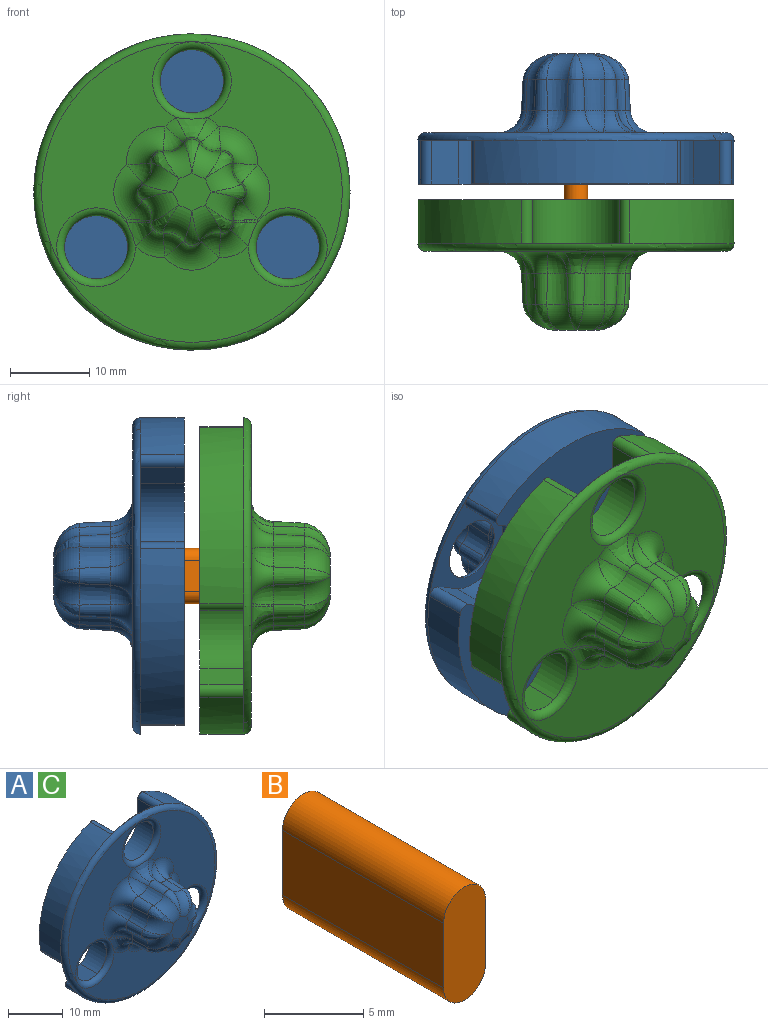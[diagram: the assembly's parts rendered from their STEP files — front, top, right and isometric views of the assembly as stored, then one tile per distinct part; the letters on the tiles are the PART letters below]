
ASSEMBLY  parts=3 mates=2
PART A: 99 faces, bbox 43.3x16.5x43.3 mm
  f0: plane 38.02x38.02mm, normal (0,-1,0), area 617.7mm2, adj f1,f47,f48,f49,f50,f89,f90,f91
  f1: torus R=4.39mm, axis (0,-1,0), area 1.4mm2, adj f0,f2,f45,f46
  f2: bspline ~3.03x2.86mm, area 5.2mm2, adj f1,f3,f47
  f3: cone r=2.36mm half-angle=3deg, axis (0,-1,0), area 11.4mm2, adj f2,f4,f44,f45
  f4: cone r=1.55mm half-angle=3deg, axis (0,1,0), area 9.6mm2, adj f3,f5,f42,f47
  f5: bspline ~4.27x3.32mm, area 5.5mm2, adj f4,f6,f44
  f6: torus R=6.21mm, axis (0,-1,0), area 14mm2, adj f5,f7,f41,f42
  f7: plane 4.83x4.83mm, normal (0,-1,0), area 15.8mm2, adj f6,f8,f35,f36,f37,f38,f39,f44
  f8: torus R=6.21mm, axis (0,-1,0), area 14mm2, adj f7,f9,f13,f14,f34
  f9: bspline ~3.02x2.67mm, area 3.8mm2, adj f8,f10,f39
  f10: cone r=1.55mm half-angle=3deg, axis (0,1,0), area 9.6mm2, adj f9,f11,f14,f95
  f11: cone r=2.36mm half-angle=3deg, axis (0,-1,0), area 11.4mm2, adj f10,f12,f39,f45
  f12: bspline ~3.03x2.86mm, area 5.2mm2, adj f11,f95,f96
  f13: bspline ~2.03x0.58mm, area 0.1mm2, adj f8,f39
  f14: cone r=2.36mm half-angle=3deg, axis (0,-1,0), area 11.4mm2, adj f8,f10,f15,f33
  f15: cone r=1.55mm half-angle=3deg, axis (0,1,0), area 9.6mm2, adj f14,f16,f17,f34,f92,f94
  f16: bspline ~4.05x3.8mm, area 7.7mm2, adj f15,f92,f93,f94
  f17: cone r=2.36mm half-angle=3deg, axis (0,-1,0), area 11.4mm2, adj f15,f18,f32,f35
  f18: cone r=1.55mm half-angle=3deg, axis (0,1,0), area 9.6mm2, adj f17,f19,f20,f91
  f19: bspline ~4.27x3.32mm, area 5.2mm2, adj f18,f35,f36
  f20: cone r=2.36mm half-angle=3deg, axis (0,-1,0), area 11.4mm2, adj f18,f21,f31,f36
  f21: cone r=1.55mm half-angle=3deg, axis (0,1,0), area 9.6mm2, adj f20,f22,f23,f90
  f22: bspline ~3.38x3.37mm, area 4.6mm2, adj f21,f36,f37
  f23: cone r=2.36mm half-angle=3deg, axis (0,-1,0), area 11.4mm2, adj f21,f24,f30,f37
  f24: cone r=1.55mm half-angle=3deg, axis (0,1,0), area 9.6mm2, adj f23,f25,f26,f27,f49,f89
  f25: bspline ~4.27x3.32mm, area 5.4mm2, adj f24,f37,f38
  f26: bspline ~4.88x3.08mm, area 9mm2, adj f24,f49,f50,f89
  f27: cone r=2.36mm half-angle=3deg, axis (0,-1,0), area 11.4mm2, adj f24,f28,f29,f38
  f28: cone r=1.55mm half-angle=3deg, axis (0,1,0), area 9.6mm2, adj f27,f41,f42,f48
  f29: bspline ~3.03x2.86mm, area 5.2mm2, adj f27,f48,f49
  f30: bspline ~3.03x2.86mm, area 5.2mm2, adj f23,f89,f90
  f31: bspline ~3.03x2.86mm, area 5.2mm2, adj f20,f90,f91
  f32: bspline ~3.03x2.86mm, area 5.2mm2, adj f17,f91,f92
  f33: bspline ~3.03x2.86mm, area 5.2mm2, adj f14,f94,f95
  f34: bspline ~3.38x3.37mm, area 4.6mm2, adj f8,f15,f35
  f35: torus R=6.21mm, axis (0,-1,0), area 14mm2, adj f7,f17,f19,f34
  f36: torus R=6.21mm, axis (0,-1,0), area 14mm2, adj f7,f19,f20,f22
  f37: torus R=6.21mm, axis (0,-1,0), area 14mm2, adj f7,f22,f23,f25
  f38: torus R=6.21mm, axis (0,-1,0), area 14mm2, adj f7,f25,f27,f41
  f39: torus R=6.21mm, axis (0,-1,0), area 14mm2, adj f7,f9,f11,f13,f40
  f40: bspline ~3.38x3.37mm, area 4.6mm2, adj f39,f44,f45
  f41: bspline ~3.38x3.37mm, area 4.6mm2, adj f6,f28,f38
  f42: cone r=2.36mm half-angle=3deg, axis (0,-1,0), area 11.4mm2, adj f4,f6,f28,f43
  f43: bspline ~3.03x2.86mm, area 5.2mm2, adj f42,f47,f48
  f44: torus R=6.21mm, axis (0,-1,0), area 14mm2, adj f3,f5,f7,f40
  f45: cone r=1.55mm half-angle=3deg, axis (0,1,0), area 9.6mm2, adj f1,f3,f11,f40,f46,f96
  f46: bspline ~4.05x3.8mm, area 7.7mm2, adj f1,f45,f96,f97
  f47: torus R=4.39mm, axis (0,-1,0), area 21.1mm2, adj f0,f2,f4,f43
  f48: torus R=4.39mm, axis (0,-1,0), area 21.1mm2, adj f0,f28,f29,f43
  f49: torus R=4.39mm, axis (0,-1,0), area 5.2mm2, adj f0,f24,f26,f29
  f50: torus R=4.99mm, axis (0,-1,0), area 42.2mm2, adj f0,f26,f51
  f51: cylinder r=4mm len=8mm, axis (0,1,0), area 0.3mm2, adj f50,f52
  f52: plane 13.66x11.5mm, normal (0,1,0), area 61.3mm2, adj f51,f53,f84,f85,f86,f87,f88
  f53: cylinder r=0.99mm len=5.5mm, axis (0,1,0), area 10.5mm2, adj f52,f54,f84,f88
  f54: plane 40x38.86mm, normal (0,1,0), area 745.2mm2, adj f53,f55,f58,f59,f60,f61,f62,f65
  f55: cylinder r=0.99mm len=5.5mm, axis (0,1,0), area 10.5mm2, adj f54,f56,f58,f88
  f56: plane 13.81x13.07mm, normal (0,1,0), area 61.3mm2, adj f55,f57,f58,f59,f60,f61,f88
  f57: cylinder r=4mm len=8mm, axis (0,1,0), area 0.3mm2, adj f56,f93
  f58: plane 5.5x3.35mm, normal (0.5,0,-0.87), area 21.3mm2, adj f54,f55,f56,f59
  f59: cylinder r=5.5mm len=10.26mm, axis (0,1,0), area 95mm2, adj f54,f56,f58,f60
  f60: plane 5.5x3.35mm, normal (-0.5,0,0.87), area 21.3mm2, adj f54,f56,f59,f61
  f61: cylinder r=0.99mm len=5.5mm, axis (0,1,0), area 10.5mm2, adj f54,f56,f60,f88
  f62: cylinder r=0.99mm len=5.5mm, axis (0,1,0), area 10.5mm2, adj f54,f63,f65,f88
  f63: plane 13.81x13.07mm, normal (0,1,0), area 61.3mm2, adj f62,f64,f65,f66,f67,f68,f88
  f64: cylinder r=4mm len=8mm, axis (0,1,0), area 0.3mm2, adj f63,f97
  f65: plane 5.5x3.35mm, normal (0.5,0,0.87), area 21.3mm2, adj f54,f62,f63,f66
  f66: cylinder r=5.5mm len=10.26mm, axis (0,1,0), area 95mm2, adj f54,f63,f65,f67
  f67: plane 5.5x3.35mm, normal (-0.5,0,-0.87), area 21.3mm2, adj f54,f63,f66,f68
  f68: cylinder r=0.99mm len=5.5mm, axis (0,1,0), area 10.5mm2, adj f54,f63,f67,f88
  f69: cylinder r=7.5mm len=15mm, axis (0,1,0), area 235.6mm2, adj f54,f70
  f70: torus R=7mm, axis (0,1,0), area 36.1mm2, adj f69,f71
  f71: plane 14x14mm, normal (0,1,0), area 75.4mm2, adj f70,f72
  f72: torus R=5mm, axis (0,1,0), area 23.1mm2, adj f71,f73
  f73: cylinder r=4.5mm len=9mm, axis (0,1,0), area 141.4mm2, adj f72,f74
  f74: plane 9x9mm, normal (0,1,0), area 28.6mm2, adj f73,f75,f81,f82,f83
  f75: torus R=2.3mm, axis (0,-1,0), area 4.9mm2, adj f74,f76,f81,f83
  f76: cylinder r=1.8mm len=5mm, axis (0,1,0), area 28.3mm2, adj f75,f77,f79,f80
  f77: plane 5x4mm, normal (1,0,0), area 20mm2, adj f76,f78,f80,f83
  f78: cylinder r=1.8mm len=5mm, axis (0,1,0), area 28.3mm2, adj f77,f79,f80,f82
  f79: plane 5x4mm, normal (-1,0,0), area 20mm2, adj f76,f78,f80,f81
  f80: plane 7.6x3.6mm, normal (0,1,0), area 24.6mm2, adj f76,f77,f78,f79
  f81: cylinder r=0.5mm len=4mm, axis (0,0,-1), area 3.1mm2, adj f74,f75,f79,f82
  f82: torus R=2.3mm, axis (0,-1,0), area 4.9mm2, adj f74,f78,f81,f83
  f83: cylinder r=0.5mm len=4mm, axis (0,0,1), area 3.1mm2, adj f74,f75,f77,f82
  f84: plane 5.5x3.87mm, normal (1,0,0), area 21.3mm2, adj f52,f53,f54,f85
  f85: cylinder r=5.5mm len=11mm, axis (0,1,0), area 95mm2, adj f52,f54,f84,f86
  f86: plane 5.5x3.87mm, normal (-1,0,0), area 21.3mm2, adj f52,f54,f85,f87
  f87: cylinder r=0.99mm len=5.5mm, axis (0,1,0), area 10.5mm2, adj f52,f54,f86,f88
  f88: cylinder r=20mm len=40mm, axis (0,1,0), area 462.5mm2, adj f52,f53,f54,f55,f56,f61,f62,f63
  f89: torus R=4.39mm, axis (0,-1,0), area 5.2mm2, adj f0,f24,f26,f30
  f90: torus R=4.39mm, axis (0,-1,0), area 21.1mm2, adj f0,f21,f30,f31
  f91: torus R=4.39mm, axis (0,-1,0), area 21.1mm2, adj f0,f18,f31,f32
  f92: torus R=4.39mm, axis (0,-1,0), area 1.4mm2, adj f0,f15,f16,f32
  f93: torus R=4.99mm, axis (0,-1,0), area 42.3mm2, adj f0,f16,f57
  f94: torus R=4.39mm, axis (0,-1,0), area 11.1mm2, adj f0,f15,f16,f33
  f95: torus R=4.39mm, axis (0,-1,0), area 21.1mm2, adj f0,f10,f12,f33
  f96: torus R=4.39mm, axis (0,-1,0), area 11.1mm2, adj f0,f12,f45,f46
  f97: torus R=4.99mm, axis (0,-1,0), area 42.3mm2, adj f0,f46,f64
  f98: torus R=19.01mm, axis (0,-1,0), area 191.9mm2, adj f0,f88
PART B: 6 faces, bbox 3x11.5x7 mm
  f0: plane 7x3mm, normal (0,-1,0), area 19.1mm2, adj f1,f2,f3,f4
  f1: plane 11.5x4mm, normal (-1,0,0), area 46mm2, adj f0,f2,f3,f5
  f2: cylinder r=1.5mm len=11.5mm, axis (0,1,0), area 54.2mm2, adj f0,f1,f4,f5
  f3: cylinder r=1.5mm len=11.5mm, axis (0,1,0), area 54.2mm2, adj f0,f1,f4,f5
  f4: plane 11.5x4mm, normal (1,0,0), area 46mm2, adj f0,f2,f3,f5
  f5: plane 7x3mm, normal (0,1,0), area 19.1mm2, adj f1,f2,f3,f4
PART C: same geometry as A
PLACE A rot(axis=(1,0,0),180deg) t=(-21.72,3.02,122.45)mm
PLACE B t=(-21.72,0.52,122.45)mm
PLACE C t=(-21.72,1.02,122.45)mm
MATE slider B.f5 <-> A.f69  axis (0,1,0) through (-21.72,7.02,122.45)mm
MATE fastened B.f0 <-> C.f69  axis (0,-1,0) through (-21.72,-4.48,122.45)mm
